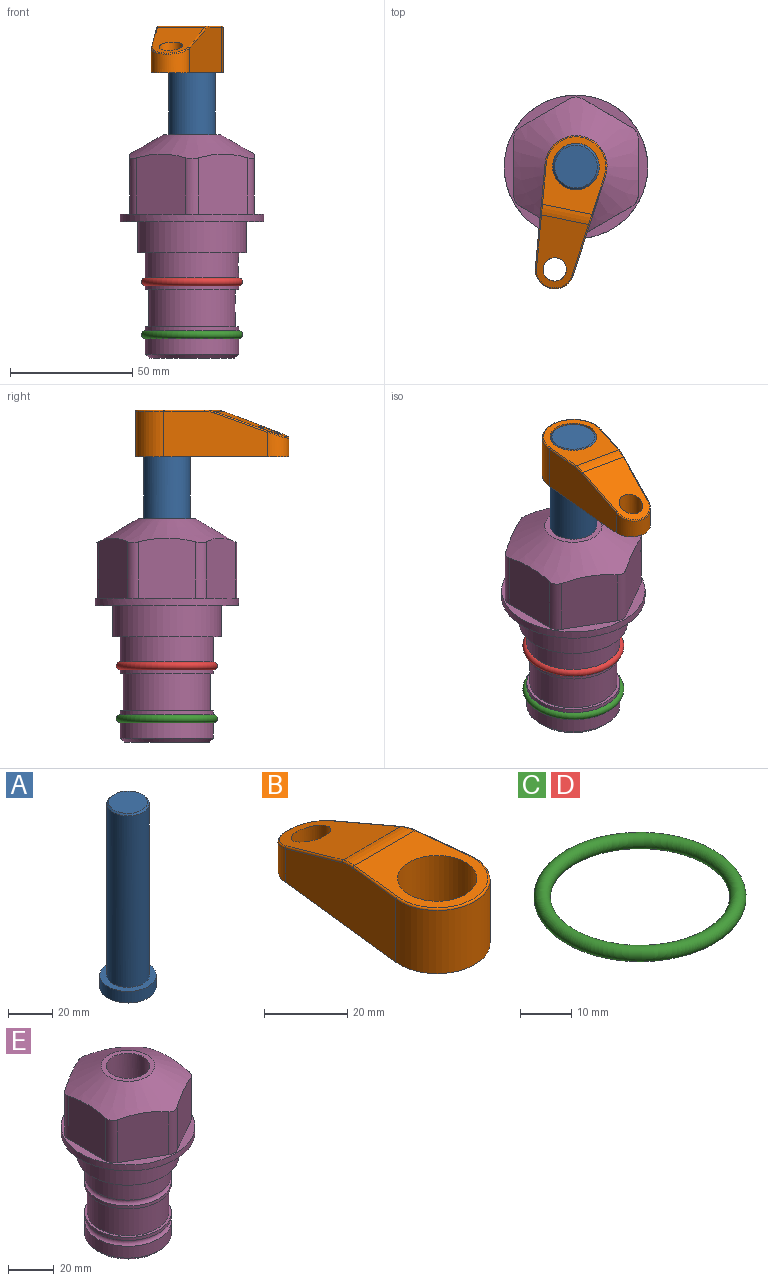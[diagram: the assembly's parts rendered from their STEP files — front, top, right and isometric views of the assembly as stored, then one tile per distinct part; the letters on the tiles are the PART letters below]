
ASSEMBLY  parts=5 mates=3
PART A: 6 faces, bbox 25.4x25.4x101.6 mm
  f0: plane 17.46x17.46mm, normal (0,0,1), area 239.5mm2, adj f5
  f1: plane 25.4x25.4mm, normal (0,0,-1), area 506.7mm2, adj f2
  f2: cylinder r=12.7mm len=25.4mm, axis (0,0,1), area 506.7mm2, adj f1,f3
  f3: plane 25.4x25.4mm, normal (0,0,1), area 221.7mm2, adj f2,f4
  f4: cylinder r=9.53mm len=94.46mm, axis (0,0,1), area 5653mm2, adj f3,f5
  f5: cone r=8.73mm half-angle=45deg, axis (0,0,-1), area 64.4mm2, adj f0,f4
PART B: 41 faces, bbox 27.5x64.5x19.1 mm
  f0: plane 63.5x25.4mm, normal (0,0,-1), area 561.7mm2, adj f1,f2,f3,f4,f5,f6,f18,f19
  f1: cylinder r=12.7mm len=25.4mm, axis (0,0,-1), area 792.2mm2, adj f0,f2,f4,f12
  f2: plane 42.33x18.54mm, normal (0.99,0.11,0), area 686.4mm2, adj f0,f1,f3,f10,f11,f13
  f3: cylinder r=7.94mm len=15.78mm, axis (0,0,-1), area 193.7mm2, adj f0,f2,f4,f15
  f4: plane 42.33x18.54mm, normal (-0.99,0.11,0), area 686.4mm2, adj f0,f1,f3,f14,f16,f17
  f5: cylinder r=9.53mm len=19.05mm, axis (0,0,-1), area 1140.1mm2, adj f0,f7
  f6: cylinder r=4.76mm len=12.5mm, axis (0,0,-1), area 321.5mm2, adj f0,f8
  f7: plane 29.99x24.38mm, normal (0,0,1), area 349.7mm2, adj f5,f9,f10,f12,f14
  f8: plane 28.32x19.62mm, normal (0,0.34,0.94), area 400.8mm2, adj f6,f9,f13,f15,f17
  f9: cylinder r=12.7mm len=20.56mm, axis (-1,0,0), area 89.1mm2, adj f7,f8,f11,f16
  f10: cylinder r=0.51mm len=16.5mm, axis (0.11,-0.99,0), area 13.2mm2, adj f2,f7,f11,f12
  f11: bspline ~4.35x1.24mm, area 3.5mm2, adj f2,f9,f10,f13
  f12: torus R=12.19mm, axis (0,0,1), area 33.6mm2, adj f1,f7,f10,f14
  f13: cylinder r=0.51mm len=21.84mm, axis (0.1,-0.93,0.34), area 18.1mm2, adj f2,f8,f11,f15
  f14: cylinder r=0.51mm len=16.5mm, axis (0.11,0.99,0), area 13.2mm2, adj f4,f7,f12,f16
  f15: bspline ~15.78x7.05mm, area 15.7mm2, adj f3,f8,f13,f17
  f16: bspline ~4.35x1.24mm, area 3.5mm2, adj f4,f9,f14,f17
  f17: cylinder r=0.51mm len=21.84mm, axis (0.1,0.93,-0.34), area 18.1mm2, adj f4,f8,f15,f16
  f18: plane 21.6x14.29mm, normal (-0.99,-0.11,0), area 268.8mm2, adj f0,f25,f27,f31,f33,f35
  f19: plane 21.6x14.29mm, normal (0.99,-0.11,0), area 268.8mm2, adj f0,f26,f28,f34,f36,f38
  f20: cylinder r=12.7mm len=14.29mm, axis (0,0,-1), area 173.4mm2, adj f0,f25,f26,f30
  f21: cylinder r=7.94mm len=9.14mm, axis (0,0,-1), area 64.6mm2, adj f0,f27,f28,f39
  f22: plane 13.14x5.11mm, normal (0,0,-1), area 50.1mm2, adj f24,f30,f31,f34
  f23: plane 13.77x11.39mm, normal (0,-0.34,-0.94), area 138.7mm2, adj f24,f35,f38,f39
  f24: cylinder r=9.53mm len=11.99mm, axis (-1,0,0), area 38.9mm2, adj f22,f23,f33,f36
  f25: cylinder r=1.59mm len=14.29mm, axis (0,0,-1), area 49mm2, adj f0,f18,f20,f29
  f26: cylinder r=1.59mm len=14.29mm, axis (0,0,-1), area 49mm2, adj f0,f19,f20,f32
  f27: cylinder r=1.59mm len=8.8mm, axis (0,0,-1), area 26.7mm2, adj f0,f18,f21,f37
  f28: cylinder r=1.59mm len=8.8mm, axis (0,0,-1), area 26.7mm2, adj f0,f19,f21,f40
  f29: sphere r=1.59mm, area 5.4mm2, adj f25,f30,f31
  f30: torus R=14.29mm, axis (0,0,1), area 31.6mm2, adj f20,f22,f29,f32
  f31: cylinder r=1.59mm len=5.29mm, axis (-0.11,0.99,0), area 12.8mm2, adj f18,f22,f29,f33
  f32: sphere r=1.59mm, area 5.4mm2, adj f26,f30,f34
  f33: bspline ~3.28x2.07mm, area 7.7mm2, adj f18,f24,f31,f35
  f34: cylinder r=1.59mm len=5.29mm, axis (0.11,0.99,0), area 12.8mm2, adj f19,f22,f32,f36
  f35: cylinder r=1.59mm len=14.16mm, axis (0.1,-0.93,0.34), area 35.9mm2, adj f18,f23,f33,f37
  f36: bspline ~3.28x2.07mm, area 7.7mm2, adj f19,f24,f34,f38
  f37: sphere r=1.59mm, area 3.6mm2, adj f27,f35,f39
  f38: cylinder r=1.59mm len=14.16mm, axis (0.1,0.93,-0.34), area 35.9mm2, adj f19,f23,f36,f40
  f39: bspline ~8.31x1.84mm, area 15.3mm2, adj f21,f23,f37,f40
  f40: sphere r=1.59mm, area 3.6mm2, adj f28,f38,f39
PART C: 1 faces, bbox 44.7x44.7x3.2 mm
  f0: torus R=19.05mm, axis (0,0,1), area 1193.9mm2
PART D: same geometry as C
PART E: 36 faces, bbox 58.7x58.7x91.2 mm
  f0: cylinder r=17.78mm len=35.56mm, axis (0,0,1), area 1670.8mm2, adj f23,f24,f31
  f1: cylinder r=19.05mm len=38.1mm, axis (0,0,1), area 1191.9mm2, adj f26,f27,f30
  f2: plane 58.66x58.66mm, normal (0,0,-1), area 1150.6mm2, adj f3,f28
  f3: cylinder r=29.33mm len=58.66mm, axis (0,0,-1), area 585.1mm2, adj f2,f4
  f4: plane 58.66x58.66mm, normal (0,0,1), area 475.9mm2, adj f3,f5,f6,f7,f8,f9,f10,f11
  f5: plane 24.5x20.32mm, normal (-0.5,0.87,0), area 562.8mm2, adj f4,f15,f16,f17
  f6: plane 24.5x20.32mm, normal (0.5,0.87,0), area 562.8mm2, adj f4,f14,f15,f17
  f7: plane 24.5x23.48mm, normal (1,0,0), area 562.8mm2, adj f4,f13,f14,f17
  f8: plane 24.5x20.32mm, normal (0.5,-0.87,0), area 562.8mm2, adj f4,f12,f13,f17
  f9: plane 24.5x20.32mm, normal (-0.5,-0.87,0), area 562.8mm2, adj f4,f11,f12,f17
  f10: plane 24.5x23.48mm, normal (-1,0,0), area 562.8mm2, adj f4,f11,f16,f17
  f11: cylinder r=5.08mm len=23.01mm, axis (0,0,-1), area 121.2mm2, adj f4,f9,f10,f17
  f12: cylinder r=5.08mm len=23.01mm, axis (0,0,-1), area 121.2mm2, adj f4,f8,f9,f17
  f13: cylinder r=5.08mm len=23.01mm, axis (0,0,-1), area 121.2mm2, adj f4,f7,f8,f17
  f14: cylinder r=5.08mm len=23.01mm, axis (0,0,-1), area 121.2mm2, adj f4,f6,f7,f17
  f15: cylinder r=5.08mm len=23.01mm, axis (0,0,-1), area 121.2mm2, adj f4,f5,f6,f17
  f16: cylinder r=5.08mm len=23.01mm, axis (0,0,-1), area 121.2mm2, adj f4,f5,f10,f17
  f17: cone r=11.73mm half-angle=60deg, axis (0,0,-1), area 2071.8mm2, adj f5,f6,f7,f8,f9,f10,f11,f12
  f18: plane 23.46x23.46mm, normal (0,0,1), area 147.4mm2, adj f17,f35
  f19: plane 34.93x34.93mm, normal (0,0,-1), area 958mm2, adj f29
  f20: cylinder r=19.05mm len=38.1mm, axis (0,0,1), area 760.1mm2, adj f21,f29
  f21: torus R=19.05mm, axis (0,0,1), area 565.3mm2, adj f20,f22
  f22: cylinder r=19.05mm len=38.1mm, axis (0,0,1), area 190mm2, adj f21,f23
  f23: plane 38.1x38.1mm, normal (0,0,1), area 146.9mm2, adj f0,f22
  f24: plane 38.1x38.1mm, normal (0,0,-1), area 146.9mm2, adj f0,f25
  f25: cylinder r=19.05mm len=38.1mm, axis (0,0,1), area 190mm2, adj f24,f26
  f26: torus R=19.05mm, axis (0,0,1), area 565.3mm2, adj f1,f25
  f27: plane 44.45x44.45mm, normal (0,0,-1), area 411.7mm2, adj f1,f28
  f28: cylinder r=22.23mm len=44.45mm, axis (0,0,1), area 1773.5mm2, adj f2,f27
  f29: cone r=19.05mm half-angle=45deg, axis (0,0,1), area 257.5mm2, adj f19,f20
  f30: cylinder r=3.17mm len=6.75mm, axis (-1,0,0), area 128mm2, adj f1,f33
  f31: cylinder r=3.17mm len=6.35mm, axis (-1,0,0), area 102.5mm2, adj f0,f33
  f32: plane 25.4x25.4mm, normal (0,0,1), area 506.7mm2, adj f33
  f33: cylinder r=12.7mm len=66.42mm, axis (0,0,-1), area 5236.2mm2, adj f30,f31,f32,f34
  f34: cone r=9.53mm half-angle=30deg, axis (0,0,-1), area 443.4mm2, adj f33,f35
  f35: cylinder r=9.53mm len=19.05mm, axis (0,0,-1), area 849mm2, adj f18,f34
PLACE A rot(axis=(0,0,-1),101.7deg) t=(0,0,6.38)mm
PLACE B rot(axis=(0,0,1),168.3deg) t=(0,0,60.99)mm
PLACE C t=(0,0,-21.59)mm
PLACE D at identity
PLACE E at identity fixed
MATE fastened C.f0 <-> E.f0  axis (0,0,1) through (0,0,-46.1)mm
MATE cylindrical A.f2 <-> E.f0  axis (0,0,1) through (0,0,32.01)mm
MATE fastened B.f1 <-> A.f2  axis (0,0,1) through (0,0,80.04)mm
